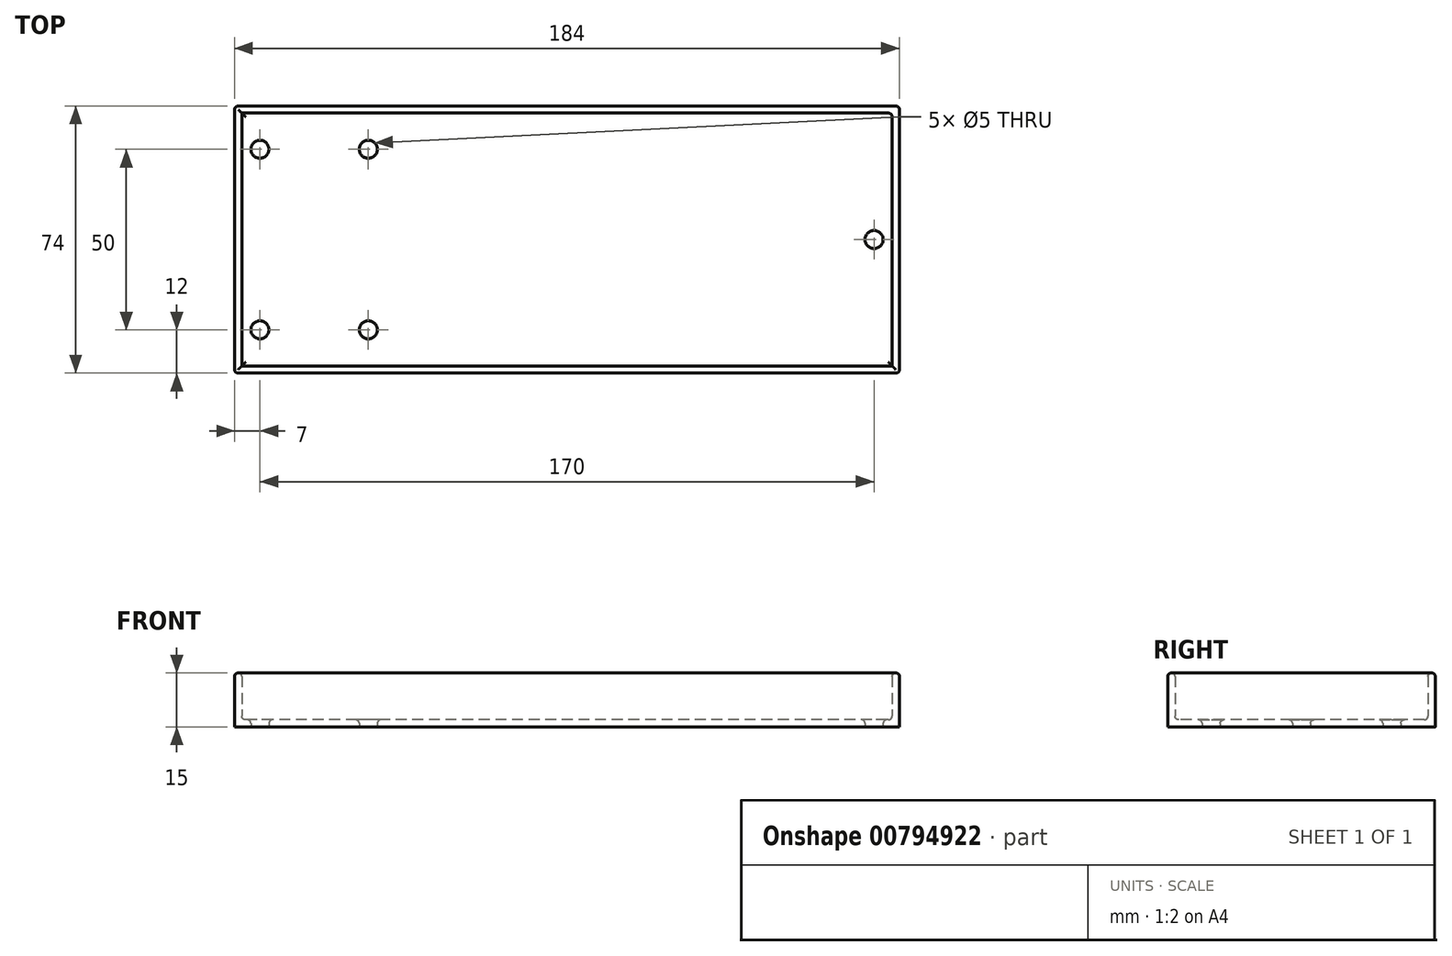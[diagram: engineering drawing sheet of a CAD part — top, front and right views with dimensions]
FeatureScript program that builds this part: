
annotation { "Feature Type Name" : "Feature", "Feature Type Description" : "" }
export const myFeature = defineFeature(function(context is Context, id is Id, definition is map)
    precondition{}
    {
        {
            var Q0;
            Q0=qCreatedBy(makeId("Top.planeOp"),FACE);
            var sketch = newSketch(context, id + "F0", { "sketchPlane" : qUnion([Q0])});
            skLineSegment(sketch, "E0.bottom", {"start": v(90, 35) * mm, "end": v(-90, 35) * mm});
            skLineSegment(sketch, "E0.top", {"start": v(90, -35) * mm, "end": v(-90, -35) * mm});
            skLineSegment(sketch, "E0.left", {"start": v(90, 35) * mm, "end": v(90, -35) * mm});
            skLineSegment(sketch, "E0.right", {"start": v(-90, 35) * mm, "end": v(-90, -35) * mm});
            skPoint(sketch, "E0.middle", {"position": v(0, 0) * mm});
            skLineSegment(sketch, "E1.0", {"start": v(-92, 37) * mm, "end": v(-92, -37) * mm});
            skLineSegment(sketch, "E1.1", {"start": v(92, 37) * mm, "end": v(-92, 37) * mm});
            skLineSegment(sketch, "E1.2", {"start": v(92, 37) * mm, "end": v(92, -37) * mm});
            skLineSegment(sketch, "E1.3", {"start": v(92, -37) * mm, "end": v(-92, -37) * mm});
            skCircle(sketch, "E2", {"center": v(-85, 25) * mm, "radius": 2.5 * mm});
            skCircle(sketch, "E3", {"center": v(-55, 25) * mm, "radius": 2.5 * mm});
            skCircle(sketch, "E4", {"center": v(-85, -25) * mm, "radius": 2.5 * mm});
            skCircle(sketch, "E5", {"center": v(-55, -25) * mm, "radius": 2.5 * mm});
            skCircle(sketch, "E6", {"center": v(85, 0) * mm, "radius": 2.5 * mm});
            skPoint(sketch, "E6.centerSnap0", {"position": v(90, 0) * mm});
            skSolve(sketch);
        }
        {
            var Q0;
            Q0=makeQuery(id+"F0.imprint","IMPRINT",FACE,{"disambiguationData":[TD([[makeQuery(id+"F0.imprint","IMPRINT",EDGE,{"derivedFrom":sQuery(id+"F0.wireOp",EDGE,"E0.bottom")}),1.0]])]});
            var Q1;
            Q1=makeQuery(id+"F0.imprint","IMPRINT",FACE,{"disambiguationData":[TD([[makeQuery(id+"F0.imprint","IMPRINT",EDGE,{"derivedFrom":sQuery(id+"F0.wireOp",EDGE,"TI2uDtPH-nBR6-LGWn-Wmlm-1JTWF2m1VAGq")}),1.0]])]});
            extrude(context, id + "F1", {"entities" : qUnion([Q0, Q1]), "depth" : 2 * mm, "offsetDistance" : 25 * mm});
        }
        {
            var Q0;
            Q0=makeQuery(id+"F0.imprint","IMPRINT",FACE,{"disambiguationData":[TD([[makeQuery(id+"F0.imprint","IMPRINT",EDGE,{"derivedFrom":sQuery(id+"F0.wireOp",EDGE,"E0.bottom")}),-1.0]])]});
            extrude(context, id + "F2", {"entities" : qUnion([Q0]), "operationType" : NewBodyOperationType.ADD, "depth" : 15 * mm, "offsetDistance" : 25 * mm});
        }
        {
            var Q0;
            Q0=makeQuery(id+"F0.imprint","IMPRINT",FACE,{"disambiguationData":[TD([[makeQuery(id+"F0.imprint","IMPRINT",EDGE,{"derivedFrom":sQuery(id+"F0.wireOp",EDGE,"E5")}),1.0]])]});
            var Q1;
            Q1=makeQuery(id+"F0.imprint","IMPRINT",FACE,{"disambiguationData":[TD([[makeQuery(id+"F0.imprint","IMPRINT",EDGE,{"derivedFrom":sQuery(id+"F0.wireOp",EDGE,"E4")}),1.0]])]});
            var Q2;
            Q2=makeQuery(id+"F0.imprint","IMPRINT",FACE,{"disambiguationData":[TD([[makeQuery(id+"F0.imprint","IMPRINT",EDGE,{"derivedFrom":sQuery(id+"F0.wireOp",EDGE,"E2")}),1.0]])]});
            var Q3;
            Q3=makeQuery(id+"F0.imprint","IMPRINT",FACE,{"disambiguationData":[TD([[makeQuery(id+"F0.imprint","IMPRINT",EDGE,{"derivedFrom":sQuery(id+"F0.wireOp",EDGE,"E3")}),1.0]])]});
            extrude(context, id + "F3", {"entities" : qUnion([Q0, Q1, Q2, Q3]), "operationType" : NewBodyOperationType.REMOVE, "oppositeDirection" : true, "depth" : 25 * mm, "offsetDistance" : 25 * mm});
        }
        {
            var Q0;
            Q0=makeQuery(id+"F2.opExtrude","SWEPT_EDGE",EDGE,{"disambiguationData":[OSD([sQuery(id+"F0.wireOp",EDGE,"E1.1"),sQuery(id+"F0.wireOp",EDGE,"E1.2")])]});
            var Q1;
            Q1=makeQuery(id+"F2.opExtrude","SWEPT_EDGE",EDGE,{"disambiguationData":[OSD([sQuery(id+"F0.wireOp",EDGE,"E0.bottom"),sQuery(id+"F0.wireOp",EDGE,"E0.left")])]});
            var Q2;
            Q2=makeQuery(id+"F2.opExtrude","CAP_FACE",FACE,{"disambiguationData":[OSD([sQuery(id+"F0.wireOp",EDGE,"E0.bottom"),sQuery(id+"F0.wireOp",EDGE,"E0.top"),sQuery(id+"F0.wireOp",EDGE,"E0.left"),sQuery(id+"F0.wireOp",EDGE,"E0.right"),sQuery(id+"F0.wireOp",EDGE,"E1.0"),sQuery(id+"F0.wireOp",EDGE,"E1.1"),sQuery(id+"F0.wireOp",EDGE,"E1.2"),sQuery(id+"F0.wireOp",EDGE,"E1.3")])],"isStart":false});
            var Q3;
            Q3=makeQuery(id+"F2.opExtrude","SWEPT_EDGE",EDGE,{"disambiguationData":[OSD([sQuery(id+"F0.wireOp",EDGE,"E1.2"),sQuery(id+"F0.wireOp",EDGE,"E1.3")])]});
            var Q4;
            Q4=makeQuery(id+"F2.opExtrude","SWEPT_EDGE",EDGE,{"disambiguationData":[OSD([sQuery(id+"F0.wireOp",EDGE,"E1.0"),sQuery(id+"F0.wireOp",EDGE,"E1.3")])]});
            var Q5;
            Q5=makeQuery(id+"F2.opExtrude","SWEPT_EDGE",EDGE,{"disambiguationData":[OSD([sQuery(id+"F0.wireOp",EDGE,"E1.0"),sQuery(id+"F0.wireOp",EDGE,"E1.1")])]});
            var Q6;
            Q6=makeQuery(id+"F1.opExtrude","CAP_FACE",FACE,{"disambiguationData":[OSD([sQuery(id+"F0.wireOp",EDGE,"E0.bottom"),sQuery(id+"F0.wireOp",EDGE,"E0.top"),sQuery(id+"F0.wireOp",EDGE,"E0.left"),sQuery(id+"F0.wireOp",EDGE,"E0.right"),sQuery(id+"F0.wireOp",EDGE,"E2"),sQuery(id+"F0.wireOp",EDGE,"E3"),sQuery(id+"F0.wireOp",EDGE,"E4"),sQuery(id+"F0.wireOp",EDGE,"E5"),sQuery(id+"F0.wireOp",EDGE,"E6")])],"isStart":false});
            fillet(context, id + "F4", {"entities" : qUnion([Q0, Q1, Q2, Q3, Q4, Q5, Q6]), "radius" : 1 * mm, "tangentPropagation" : true, "allowEdgeOverflow" : false});
        }
    });
